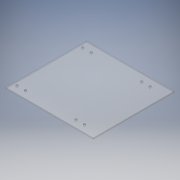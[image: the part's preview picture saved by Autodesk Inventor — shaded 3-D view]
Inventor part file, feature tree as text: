
AUTODESK INVENTOR PART (.ipt)
format: ipt  version: 2019 (Build 230136000, 136)  size: 124,928 bytes
history: native  units: in
note: dims shown in document units (in); Inventor stores cm internally (conversion verified against a paired STEP export)
features: sketch x2, extrude x1, hole x1, projected_geometry x1
ambient origin geometry x8: Origin, YZ Plane, XZ Plane, XY Plane, X Axis, Y Axis, Z Axis, Center Point
bodies: Solid1 (feature_tree)
feature tree (5):
  extrude  "Extrusion1"  Depth=6.0in
  hole  "Hole1"  [1 undecoded]
  sketch  "Sketch1"  dims[d0=6.5in d1=6.0in]
  sketch  "Sketch2"  dims[d2=0.073in d3=0.0in d4=6.5in d5=0.6299in d6=0.6299in d7=0.6299in d8=0.6299in d9=0.557in d10=0.557in d11=0.557in d12=0.557in d13=0.557in d14=0.557in d15=0.557in d16=0.557in d17=1.847in d18=1.847in d19=6.23in d20=6.23in d21=0.15in d22=0.75in d23=0.375in d24=0.25in d25=0.5635in d26=0.432in d27=0.8108in]
  projected_geometry  "Projected Loop1"
note: 1 required parameter value undecoded (feature->parameter linkage not recoverable at this tier; creation-order binding heuristic only, values carry confidence <= 0.55)
